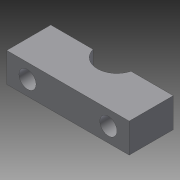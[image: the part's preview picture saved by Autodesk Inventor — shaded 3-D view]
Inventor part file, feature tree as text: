
AUTODESK INVENTOR PART (.ipt)
format: ipt  version: 2014 (Build 180170000, 170)  size: 102,912 bytes
history: native  units: mm
features: extrude x3, sketch x3, projected_geometry x1
ambient origin geometry x8: Origin, YZ Plane, XZ Plane, XY Plane, X Axis, Y Axis, Z Axis, Center Point
bodies: Solid1 (feature_tree)
feature tree (7):
  extrude  "Extrusion1"  Depth=10.0mm
  extrude  "Extrusion2"  Depth=6.0mm TaperAngle=0.0deg
  extrude  "Extrusion3"  Depth=6.0mm TaperAngle=0.0deg
  sketch  "Sketch1"  dims[d0=4.0mm d1=10.0mm]
  sketch  "Sketch2"  dims[d2=25.0mm d3=6.0mm d4=0.0mm]
  projected_geometry  "Projected Loop1"
  sketch  "Sketch3"  dims[d5=3.5mm d6=6.0mm d7=0.0mm d8=1.0mm d9=10.0mm d10=0.0mm]
